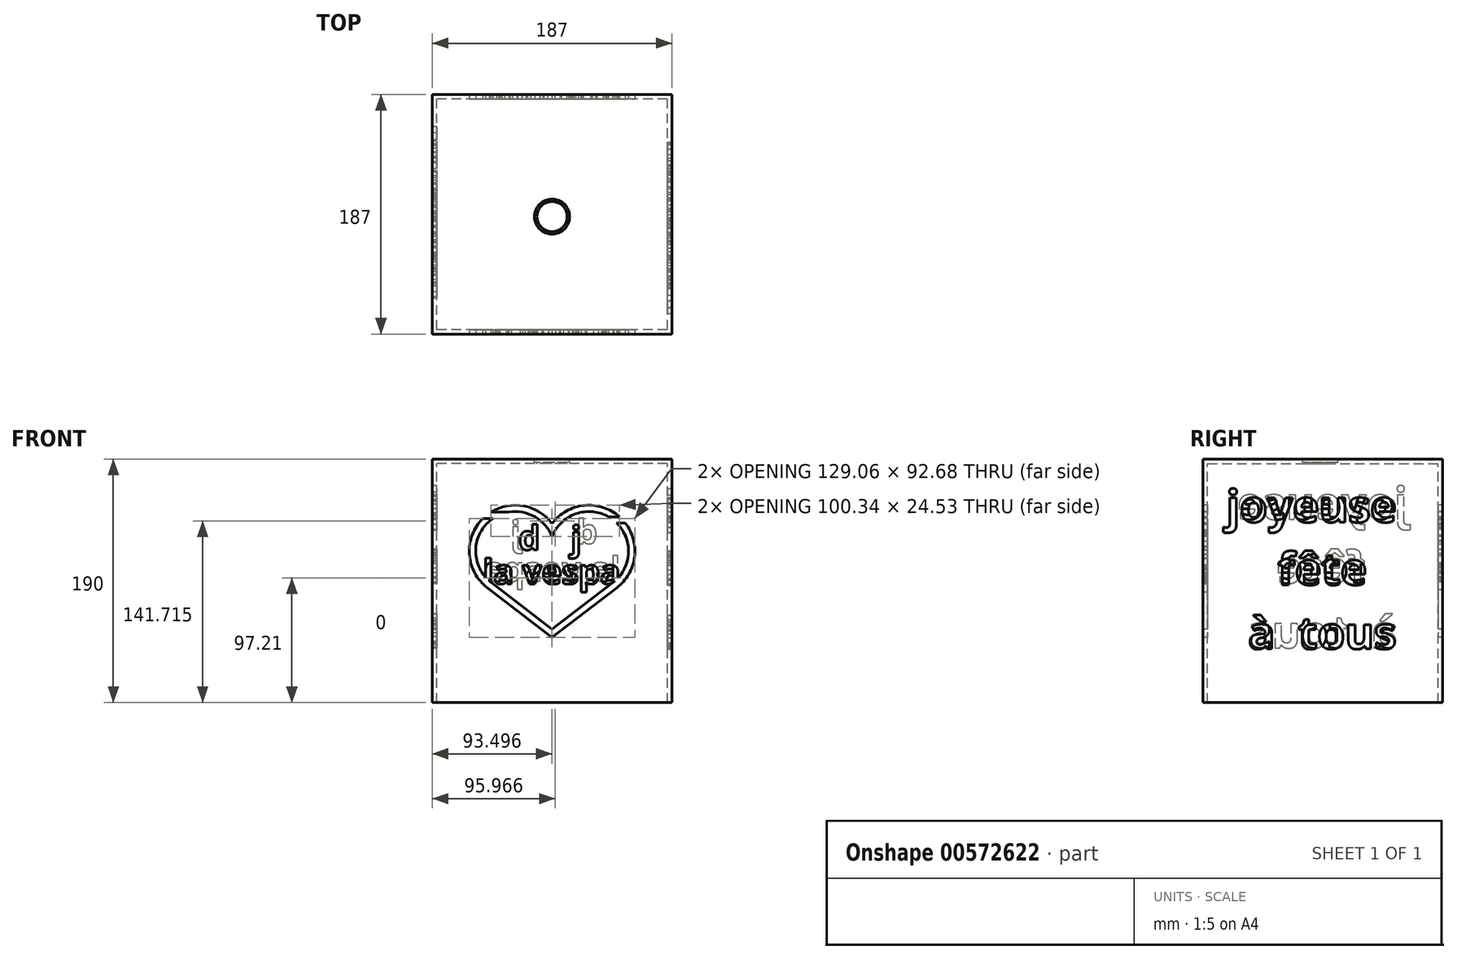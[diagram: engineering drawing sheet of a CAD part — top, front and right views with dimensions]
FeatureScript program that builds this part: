
annotation { "Feature Type Name" : "Feature", "Feature Type Description" : "" }
export const myFeature = defineFeature(function(context is Context, id is Id, definition is map)
    precondition{}
    {
        {
            var Q0;
            Q0=qCreatedBy(makeId("Top.planeOp"),FACE);
            var sketch = newSketch(context, id + "F0", { "sketchPlane" : qUnion([Q0])});
            skLineSegment(sketch, "E0.bottom", {"start": v(-93.5, 95.35) * mm, "end": v(93.5, 95.35) * mm});
            skLineSegment(sketch, "E0.top", {"start": v(-93.5, -91.65) * mm, "end": v(93.5, -91.65) * mm});
            skLineSegment(sketch, "E0.left", {"start": v(-93.5, 95.35) * mm, "end": v(-93.5, -91.65) * mm});
            skLineSegment(sketch, "E0.right", {"start": v(93.5, 95.35) * mm, "end": v(93.5, -91.65) * mm});
            skSolve(sketch);
        }
        {
            var Q0;
            Q0=makeQuery(id+"F0.imprint","IMPRINT",FACE,{"disambiguationData":[TD([[makeQuery(id+"F0.imprint","IMPRINT",EDGE,{"derivedFrom":sQuery(id+"F0.wireOp",EDGE,"E0.bottom")}),-1.0]])]});
            extrude(context, id + "F1", {"entities" : qUnion([Q0]), "depth" : 190 * mm, "offsetDistance" : 25 * mm});
        }
        {
            var Q0;
            Q0=makeQuery(id+"F1.opExtrude","CAP_FACE",FACE,{"disambiguationData":[OSD([sQuery(id+"F0.wireOp",EDGE,"E0.bottom"),sQuery(id+"F0.wireOp",EDGE,"E0.top"),sQuery(id+"F0.wireOp",EDGE,"E0.left"),sQuery(id+"F0.wireOp",EDGE,"E0.right")])],"isStart":false});
            var sketch = newSketch(context, id + "F2", { "sketchPlane" : qUnion([Q0])});
            skLineSegment(sketch, "E1.0", {"start": v(-93.5, 91.85) * mm, "end": v(93.5, 91.85) * mm});
            skLineSegment(sketch, "E2.0", {"start": v(90, 95.35) * mm, "end": v(90, -91.65) * mm});
            skLineSegment(sketch, "E3.0", {"start": v(-93.5, -88.15) * mm, "end": v(93.5, -88.15) * mm});
            skLineSegment(sketch, "E4.0", {"start": v(-90, 95.35) * mm, "end": v(-90, -91.65) * mm});
            skSolve(sketch);
        }
        {
            var Q0;
            {var subQ0=sQuery(id+"F2.wireOp",EDGE,"E4.0");var subQ1=sQuery(id+"F2.wireOp",EDGE,"E1.0");var subQ2=makeQuery(id+"F2.imprint","INTERSECT",VERTEX,{"derivedFrom":[subQ1,subQ0]});Q0=makeQuery(id+"F2.imprint","IMPRINT",FACE,{"disambiguationData":[TD([[makeQuery(id+"F2.imprint","IMPRINT",EDGE,{"disambiguationData":[TD([[subQ2,-1.0]])],"derivedFrom":subQ1}),-1.0]])]});}
            extrude(context, id + "F3", {"entities" : qUnion([Q0]), "operationType" : NewBodyOperationType.REMOVE, "oppositeDirection" : true, "depth" : 190 * mm, "offsetDistance" : 25 * mm});
        }
        {
            var Q0;
            Q0=makeQuery(id+"F1.opExtrude","SWEPT_FACE",FACE,{"disambiguationData":[OSD([sQuery(id+"F0.wireOp",EDGE,"E0.right")])]});
            var sketch = newSketch(context, id + "F4", { "sketchPlane" : qUnion([Q0])});
            skText(sketch, "E5", { "text": "joyeuse", "fontName": "OpenSans-Bold.ttf"});
            skText(sketch, "E6", { "text": "fête", "fontName": "OpenSans-Bold.ttf"});
            skText(sketch, "E7", { "text": "à  tous", "fontName": "OpenSans-Bold.ttf"});
            const initialGuessF4  = {"E5": [-0.0735, 0.14072, 1, 0, 0.025], "E6": [-0.0333, 0.09183, 1, 0, 0.025], "E7": [-0.05645, 0.04183, 1, 0, 0.025]};
            skSetInitialGuess(sketch, initialGuessF4);
            skSolve(sketch);
        }
        {
            var Q0;
            Q0=makeQuery(id+"F1.opExtrude","SWEPT_FACE",FACE,{"disambiguationData":[OSD([sQuery(id+"F0.wireOp",EDGE,"E0.left")])]});
            var sketch = newSketch(context, id + "F5", { "sketchPlane" : qUnion([Q0])});
            skText(sketch, "E8", { "text": "joyeuse", "fontName": "OpenSans-Bold.ttf"});
            skText(sketch, "E9", { "text": "fête", "fontName": "OpenSans-Bold.ttf"});
            skText(sketch, "E10", { "text": "à  tous", "fontName": "OpenSans-Bold.ttf"});
            const initialGuessF5  = {"E8": [-0.06797, 0.14293, 1, 0, 0.025], "E9": [-0.03515, 0.0931, 1, 0, 0.025], "E10": [-0.06016, 0.04266, 1, 0, 0.025]};
            skSetInitialGuess(sketch, initialGuessF5);
            skSolve(sketch);
        }
        {
            var Q0;
            Q0=qSketchRegion(id+"F5",true);
            var Q1;
            Q1=qSketchRegion(id+"F4",true);
            var Q2;
            Q2=qSketchRegion(id+"FytjR2NVyljPgOM_1",true);
            extrude(context, id + "F6", {"entities" : qUnion([Q0, Q1, Q2]), "operationType" : NewBodyOperationType.REMOVE, "oppositeDirection" : true, "depth" : 3.5 * mm, "offsetDistance" : 25 * mm});
        }
        {
            var Q0;
            Q0=qSketchRegion(id+"F4",true);
            extrude(context, id + "F7", {"entities" : qUnion([Q0]), "operationType" : NewBodyOperationType.REMOVE, "oppositeDirection" : true, "depth" : 3.5 * mm, "offsetDistance" : 25 * mm});
        }
        {
            var Q0;
            Q0=makeQuery(id+"F1.opExtrude","SWEPT_FACE",FACE,{"disambiguationData":[OSD([sQuery(id+"F0.wireOp",EDGE,"E0.top")])]});
            var sketch = newSketch(context, id + "F8", { "sketchPlane" : qUnion([Q0])});
            skLineSegment(sketch, "E11", {"start": v(0, 0) * mm, "end": v(0, 190) * mm, "construction": true});
            skArc(sketch, "E12", {"start": v(0, 139.6) * mm, "mid": v(-22.11, 153.36) * mm, "end": v(-47.7, 148.55) * mm});
            skLineSegment(sketch, "E13", {"start": v(-50.55, 89.6) * mm, "end": v(0, 50.87) * mm});
            skArc(sketch, "E14.MirrorCS", {"start": v(0, 139.6) * mm, "mid": v(25.17, 153.8) * mm, "end": v(52.64, 144.85) * mm});
            skLineSegment(sketch, "E15.MirrorCS", {"start": v(50.55, 89.6) * mm, "end": v(0, 50.87) * mm});
            skLineSegment(sketch, "E16.0", {"start": v(-47.5, 93.57) * mm, "end": v(0, 57.17) * mm});
            skArc(sketch, "E16.1", {"start": v(0, 129.45) * mm, "mid": v(-13.55, 145) * mm, "end": v(-33.86, 148.55) * mm});
            skArc(sketch, "E16.2", {"start": v(0, 129.45) * mm, "mid": v(18.55, 147.25) * mm, "end": v(44.15, 144.85) * mm});
            skLineSegment(sketch, "E16.3", {"start": v(47.5, 93.57) * mm, "end": v(0, 57.17) * mm});
            skLineSegment(sketch, "E17.bottom", {"start": v(-47.7, 148.55) * mm, "end": v(-33.86, 148.55) * mm});
            skLineSegment(sketch, "E17.top", {"start": v(-54.02, 143.55) * mm, "end": v(-46.21, 143.55) * mm});
            skArc(sketch, "E18.trimOffspring", {"start": v(-54.02, 143.55) * mm, "mid": v(-64.54, 115.79) * mm, "end": v(-50.55, 89.6) * mm});
            skArc(sketch, "E19.trimOffspring", {"start": v(-46.21, 143.55) * mm, "mid": v(-59.6, 118.89) * mm, "end": v(-47.5, 93.57) * mm});
            skLineSegment(sketch, "E20.bottom", {"start": v(44.15, 144.85) * mm, "end": v(52.64, 144.85) * mm});
            skLineSegment(sketch, "E20.top", {"start": v(50.44, 140.05) * mm, "end": v(57.1, 140.05) * mm});
            skArc(sketch, "E21.trimOffspring", {"start": v(50.44, 140.05) * mm, "mid": v(59.55, 116.15) * mm, "end": v(47.5, 93.57) * mm});
            skArc(sketch, "E22.trimOffspring", {"start": v(57.1, 140.05) * mm, "mid": v(64.31, 113.47) * mm, "end": v(50.55, 89.6) * mm});
            skSolve(sketch);
        }
        {
            var Q0;
            Q0=qSketchRegion(id+"F8",true);
            extrude(context, id + "F9", {"entities" : qUnion([Q0]), "operationType" : NewBodyOperationType.REMOVE, "endBound" : BoundingType.THROUGH_ALL, "oppositeDirection" : true, "depth" : 25 * mm, "offsetDistance" : 25 * mm});
        }
        {
            var Q0;
            Q0=makeQuery(id+"F1.opExtrude","SWEPT_FACE",FACE,{"disambiguationData":[OSD([sQuery(id+"F0.wireOp",EDGE,"E0.bottom")])]});
            var sketch = newSketch(context, id + "F10", { "sketchPlane" : qUnion([Q0])});
            skText(sketch, "E23", { "text": "d", "fontName": "OpenSans-Bold.ttf"});
            skPoint(sketch, "E24", {"position": v(-35.5, 88.93) * mm});
            skText(sketch, "E25", { "text": "j", "fontName": "OpenSans-Bold.ttf"});
            skText(sketch, "E26", { "text": "la vespa", "fontName": "OpenSans-Bold.ttf"});
            const initialGuessF10  = {"E23": [-0.0355, 0.12398, 1, 0, 0.019], "E25": [0.02456, 0.12266, 1, 0, 0.019], "E26": [-0.05347, 0.09455, 1, 0, 0.019]};
            skSetInitialGuess(sketch, initialGuessF10);
            skSolve(sketch);
        }
        {
            var Q0;
            Q0=qSketchRegion(id+"F10",true);
            extrude(context, id + "F11", {"entities" : qUnion([Q0]), "operationType" : NewBodyOperationType.REMOVE, "oppositeDirection" : true, "depth" : 3.5 * mm, "offsetDistance" : 25 * mm});
        }
        {
            var Q0;
            Q0=makeQuery(id+"F1.opExtrude","SWEPT_FACE",FACE,{"disambiguationData":[OSD([sQuery(id+"F0.wireOp",EDGE,"E0.top")])]});
            var sketch = newSketch(context, id + "F12", { "sketchPlane" : qUnion([Q0])});
            skText(sketch, "E27", { "text": "d", "fontName": "OpenSans-Bold.ttf"});
            skPoint(sketch, "E28", {"position": v(-26.12, 68.56) * mm});
            skText(sketch, "E29", { "text": "j", "fontName": "OpenSans-Bold.ttf"});
            skText(sketch, "E30", { "text": "la vespa", "fontName": "OpenSans-Bold.ttf"});
            const initialGuessF12  = {"E27": [-0.02612, 0.11912, 1, 0, 0.019], "E29": [0.01477, 0.11862, 1, 0, 0.019], "E30": [-0.05387, 0.09255, 1, 0, 0.019]};
            skSetInitialGuess(sketch, initialGuessF12);
            skSolve(sketch);
        }
        {
            var Q0;
            Q0=qSketchRegion(id+"F12",true);
            extrude(context, id + "F13", {"entities" : qUnion([Q0]), "operationType" : NewBodyOperationType.REMOVE, "oppositeDirection" : true, "depth" : 3.5 * mm, "offsetDistance" : 25 * mm});
        }
        {
            var Q0;
            Q0=makeQuery(id+"F1.opExtrude","CAP_FACE",FACE,{"disambiguationData":[OSD([sQuery(id+"F0.wireOp",EDGE,"E0.bottom"),sQuery(id+"F0.wireOp",EDGE,"E0.top"),sQuery(id+"F0.wireOp",EDGE,"E0.left"),sQuery(id+"F0.wireOp",EDGE,"E0.right")])],"isStart":false});
            var sketch = newSketch(context, id + "F14", { "sketchPlane" : qUnion([Q0])});
            skLineSegment(sketch, "E31.bottom", {"start": v(-93.5, 95.35) * mm, "end": v(93.5, 95.35) * mm});
            skLineSegment(sketch, "E31.top", {"start": v(-93.5, -91.65) * mm, "end": v(93.5, -91.65) * mm});
            skLineSegment(sketch, "E31.left", {"start": v(-93.5, 95.35) * mm, "end": v(-93.5, -91.65) * mm});
            skLineSegment(sketch, "E31.right", {"start": v(93.5, 95.35) * mm, "end": v(93.5, -91.65) * mm});
            skSolve(sketch);
        }
        {
            var Q0;
            Q0=qSketchRegion(id+"F14",true);
            extrude(context, id + "F15", {"entities" : qUnion([Q0]), "operationType" : NewBodyOperationType.ADD, "oppositeDirection" : true, "depth" : 3.5 * mm, "offsetDistance" : 25 * mm});
        }
        {
            var Q0;
            Q0=makeQuery(id+"F15.boolean.opBoolean","MERGE",FACE,{"derivedFrom":[makeQuery(id+"F1.opExtrude","CAP_FACE",FACE,{"disambiguationData":[OSD([sQuery(id+"F0.wireOp",EDGE,"E0.bottom"),sQuery(id+"F0.wireOp",EDGE,"E0.top"),sQuery(id+"F0.wireOp",EDGE,"E0.left"),sQuery(id+"F0.wireOp",EDGE,"E0.right")])],"isStart":false}),makeQuery(id+"F15.opExtrude","CAP_FACE",FACE,{"disambiguationData":[OSD([sQuery(id+"F14.wireOp",EDGE,"E31.bottom"),sQuery(id+"F14.wireOp",EDGE,"E31.top"),sQuery(id+"F14.wireOp",EDGE,"E31.left"),sQuery(id+"F14.wireOp",EDGE,"E31.right")])],"isStart":true})]});
            var sketch = newSketch(context, id + "F16", { "sketchPlane" : qUnion([Q0])});
            skCircle(sketch, "E32", {"center": v(0, 0) * mm, "radius": 11.75 * mm});
            skSolve(sketch);
        }
        {
            var Q0;
            Q0=qSketchRegion(id+"F16",true);
            extrude(context, id + "F17", {"entities" : qUnion([Q0]), "operationType" : NewBodyOperationType.REMOVE, "oppositeDirection" : true, "depth" : 25 * mm, "offsetDistance" : 25 * mm});
        }
        {
            var Q0;
            Q0=makeQuery(id+"F15.boolean.opBoolean","MERGE",FACE,{"derivedFrom":[makeQuery(id+"F1.opExtrude","CAP_FACE",FACE,{"disambiguationData":[OSD([sQuery(id+"F0.wireOp",EDGE,"E0.bottom"),sQuery(id+"F0.wireOp",EDGE,"E0.top"),sQuery(id+"F0.wireOp",EDGE,"E0.left"),sQuery(id+"F0.wireOp",EDGE,"E0.right")])],"isStart":false}),makeQuery(id+"F15.opExtrude","CAP_FACE",FACE,{"disambiguationData":[OSD([sQuery(id+"F14.wireOp",EDGE,"E31.bottom"),sQuery(id+"F14.wireOp",EDGE,"E31.top"),sQuery(id+"F14.wireOp",EDGE,"E31.left"),sQuery(id+"F14.wireOp",EDGE,"E31.right")])],"isStart":true})]});
            var sketch = newSketch(context, id + "F18", { "sketchPlane" : qUnion([Q0])});
            skCircle(sketch, "E33", {"center": v(0, 0) * mm, "radius": 13.75 * mm});
            skSolve(sketch);
        }
        {
            var Q0;
            Q0=qSketchRegion(id+"F18",true);
            extrude(context, id + "F19", {"entities" : qUnion([Q0]), "operationType" : NewBodyOperationType.REMOVE, "oppositeDirection" : true, "depth" : 2.5 * mm, "offsetDistance" : 25 * mm});
        }
    });
